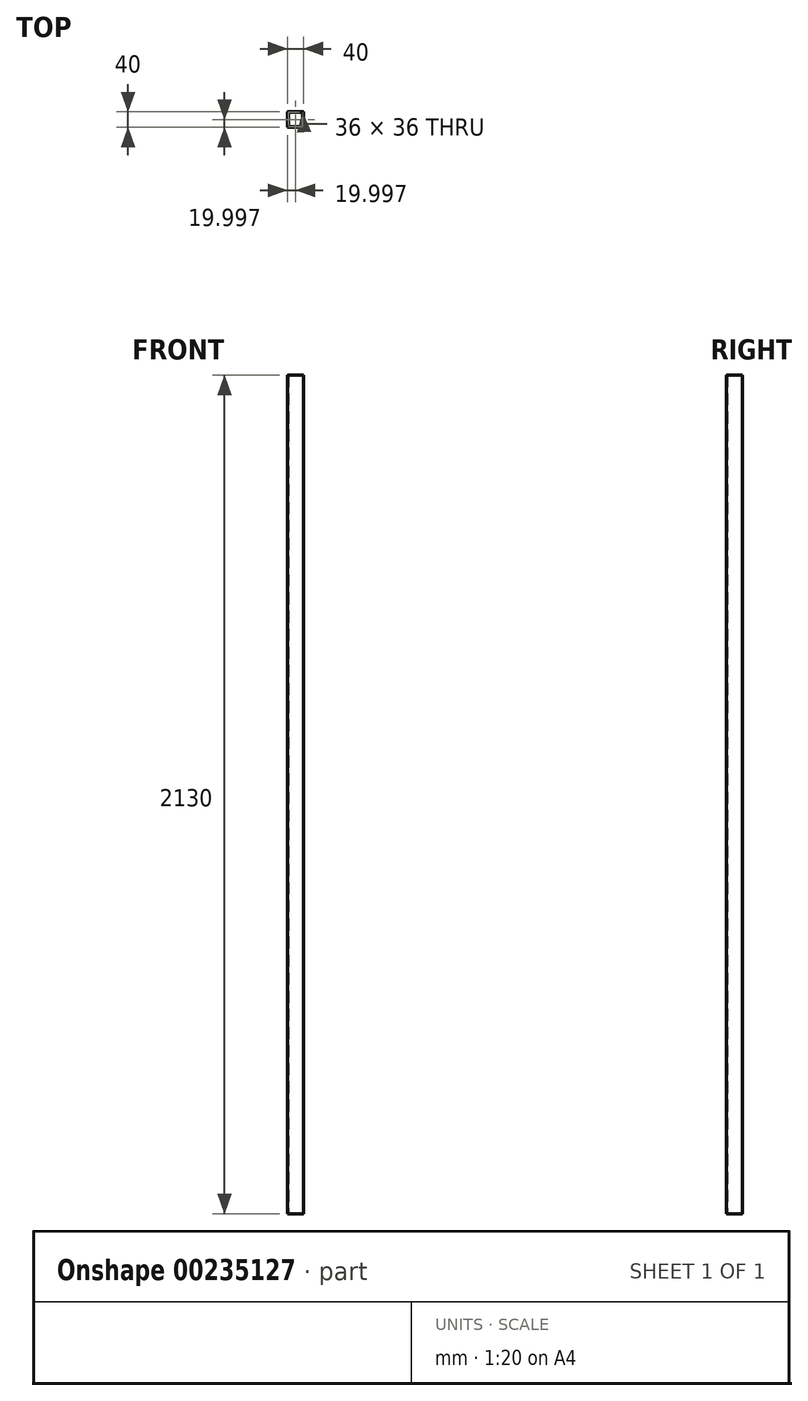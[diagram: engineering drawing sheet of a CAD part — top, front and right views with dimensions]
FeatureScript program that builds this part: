
annotation { "Feature Type Name" : "Feature", "Feature Type Description" : "" }
export const myFeature = defineFeature(function(context is Context, id is Id, definition is map)
    precondition{}
    {
        {
            var Q0;
            Q0=qCreatedBy(makeId("Top.planeOp"),FACE);
            var sketch = newSketch(context, id + "F0", { "sketchPlane" : qUnion([Q0])});
            skLineSegment(sketch, "E0.bottom", {"start": v(-11.1, 11.58) * mm, "end": v(26.9, 11.58) * mm});
            skLineSegment(sketch, "E0.top", {"start": v(-11.1, -28.42) * mm, "end": v(26.9, -28.42) * mm});
            skLineSegment(sketch, "E0.left", {"start": v(-12.1, 10.58) * mm, "end": v(-12.1, -27.42) * mm});
            skLineSegment(sketch, "E0.right", {"start": v(27.9, 10.58) * mm, "end": v(27.9, -27.42) * mm});
            skPoint(sketch, "E1.visualSharp", {"position": v(-12.1, 11.58) * mm});
            skArc(sketch, "E1.filletArc", {"start": v(-11.1, 11.58) * mm, "mid": v(-11.8, 11.28) * mm, "end": v(-12.1, 10.58) * mm});
            skPoint(sketch, "E2.visualSharp", {"position": v(27.9, 11.58) * mm});
            skArc(sketch, "E2.filletArc", {"start": v(27.9, 10.58) * mm, "mid": v(27.61, 11.28) * mm, "end": v(26.9, 11.58) * mm});
            skPoint(sketch, "E3.visualSharp", {"position": v(27.9, -28.42) * mm});
            skArc(sketch, "E3.filletArc", {"start": v(26.9, -28.42) * mm, "mid": v(27.61, -28.13) * mm, "end": v(27.9, -27.42) * mm});
            skPoint(sketch, "E4.visualSharp", {"position": v(-12.1, -28.42) * mm});
            skArc(sketch, "E4.filletArc", {"start": v(-12.1, -27.42) * mm, "mid": v(-11.8, -28.13) * mm, "end": v(-11.1, -28.42) * mm});
            skLineSegment(sketch, "E5.0", {"start": v(-10.1, 9.58) * mm, "end": v(-10.1, -26.42) * mm});
            skLineSegment(sketch, "E5.1", {"start": v(-10.1, 9.58) * mm, "end": v(25.9, 9.58) * mm});
            skLineSegment(sketch, "E5.2", {"start": v(25.9, 9.58) * mm, "end": v(25.9, -26.42) * mm});
            skLineSegment(sketch, "E5.3", {"start": v(-10.1, -26.42) * mm, "end": v(25.9, -26.42) * mm});
            skSolve(sketch);
        }
        {
            var Q0;
            Q0 = qSketchRegion(id + "F0", true);
            extrude(context, id + "F1", {"entities" : qUnion([Q0]), "depth" : 2130 * mm});
        }
    });
